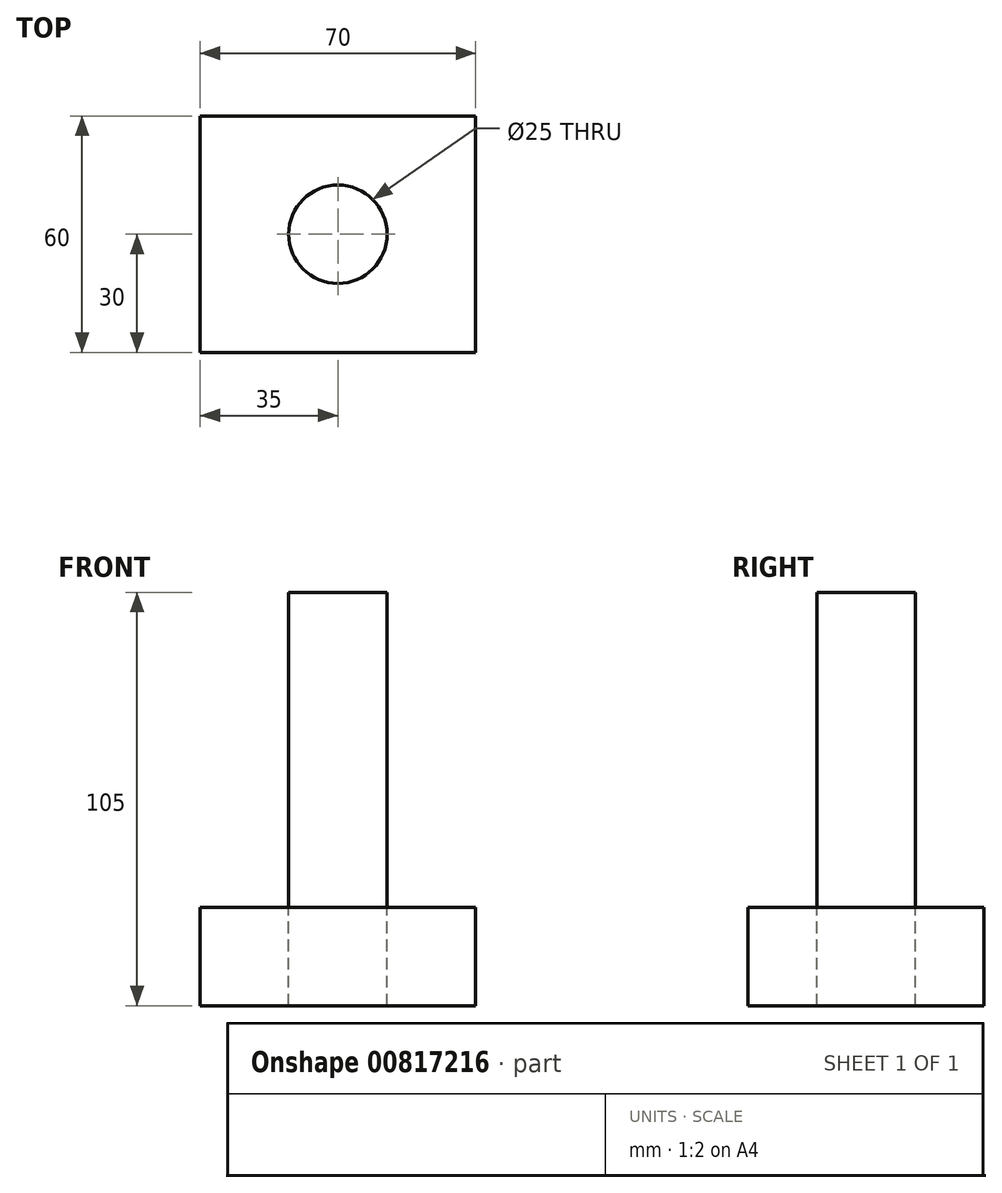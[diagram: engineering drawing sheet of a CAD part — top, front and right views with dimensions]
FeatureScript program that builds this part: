
annotation { "Feature Type Name" : "Feature", "Feature Type Description" : "" }
export const myFeature = defineFeature(function(context is Context, id is Id, definition is map)
    precondition{}
    {
        {
            var Q0;
            Q0=qCreatedBy(makeId("Top.planeOp"),FACE);
            var sketch = newSketch(context, id + "F0", { "sketchPlane" : qUnion([Q0])});
            skCircle(sketch, "E0", {"center": v(0, 0) * mm, "radius": 12.5 * mm});
            skLineSegment(sketch, "E1.bottom", {"start": v(-35, 30) * mm, "end": v(35, 30) * mm});
            skLineSegment(sketch, "E1.top", {"start": v(-35, -30) * mm, "end": v(35, -30) * mm});
            skLineSegment(sketch, "E1.left", {"start": v(-35, 30) * mm, "end": v(-35, -30) * mm});
            skLineSegment(sketch, "E1.right", {"start": v(35, 30) * mm, "end": v(35, -30) * mm});
            skSolve(sketch);
        }
        {
            var Q0;
            Q0 = qSketchRegion(id + "F0", true);
            extrude(context, id + "F1", {"entities" : qUnion([Q0]), "oppositeDirection" : true, "depth" : 25 * mm, "offsetDistance" : 25 * mm});
        }
        {
            var Q0;
            Q0=makeQuery(id+"F1.opExtrude","CAP_FACE",FACE,{"disambiguationData":[OSD([sQuery(id+"F0.wireOp",EDGE,"E0"),sQuery(id+"F0.wireOp",EDGE,"E1.bottom"),sQuery(id+"F0.wireOp",EDGE,"E1.top"),sQuery(id+"F0.wireOp",EDGE,"E1.left"),sQuery(id+"F0.wireOp",EDGE,"E1.right")])],"isStart":true});
            var sketch = newSketch(context, id + "F2", { "sketchPlane" : qUnion([Q0])});
            skCircle(sketch, "E2", {"center": v(0, 0) * mm, "radius": 12.5 * mm});
            skSolve(sketch);
        }
        {
            var Q0;
            Q0 = qSketchRegion(id + "F2", true);
            extrude(context, id + "F3", {"entities" : qUnion([Q0]), "depth" : 80 * mm, "offsetDistance" : 25 * mm});
        }
    });
